# Revit family: PFSB1500xx
name_source: partatom
category: Leuchten
units: mm (PartAtom-declared; Revit-internal decimal feet)

## family parameters
Basisbauteil = Fläche
Beim Laden mit Abzugskörper schneiden = Nein
Bemaßung runder Anschluss = Durchmesser verwenden
Gemeinsam genutzt = Nein
Lichtquelle = Ja
OmniClass-Nummer = 23.80.70.11
OmniClass-Titel = Luminaries for Internal Lighting
Raumberechnungspunkt = Nein
Teiletyp = Normal

## types (3) — shared parameters
Baugruppenkennzeichen = D5020200
Datei für fotometrisches Netz = PFSB1500.IES
Emissionsform beim Rendern sichtbar = Nein
Farbfilter = 16777215
Farbtemperaturverschiebung bei Dämpfen der Lampe = <Keine Auswahl>
Hersteller = RIDI Leuchten GmbH
Lampe = LED
Neigungswinkel = 90.00°
Scheinlast = 50 VA
URL = www.ridi.de
Von Breite des Rechtecks ausssenden = 1470 mm
Von Länge des Rechtecks aussenden = 55 mm  [stored 0.180446 ft]
brand = RIDI
conformity mark = CE
electrical safety class = 1
height = 77 mm  [stored 0.252625 ft]
ingress protection (IP) code = IP65
length = 1620 mm
nominal frequency = 50-60Hz
nominal voltage = 230
rated input power = 50
voltage type (AC, DC, UC) = AC
weight = 1,65
width = 66 mm  [stored 0.216535 ft]
zero-valued in all types: Vorgabe-Ansicht

## per-type parameters (varying)
| type | Modell | product name |
| PFSB1500NDLG840O0600 | 0921233BH | PFSB1500NDLG840O0600
EL-AQ0622NDWS840M9P0400
EL-AQ0622DAWS840M9S0350 |
| PFSB1500DALG840O0600 | 0931233BH | PFSB1500DALG840O0600
EL-AQ0622NDWS840M9P0400
EL-AQ0622DAWS840M9S0350 |
| PFSB1500NDLG840O0600-RS | 0921234BH | PFSB1500NDLG840O0600-RS |

note: [stored X ft] marks values corroborated as IEEE doubles in the binary element streams (Revit-internal decimal feet)
